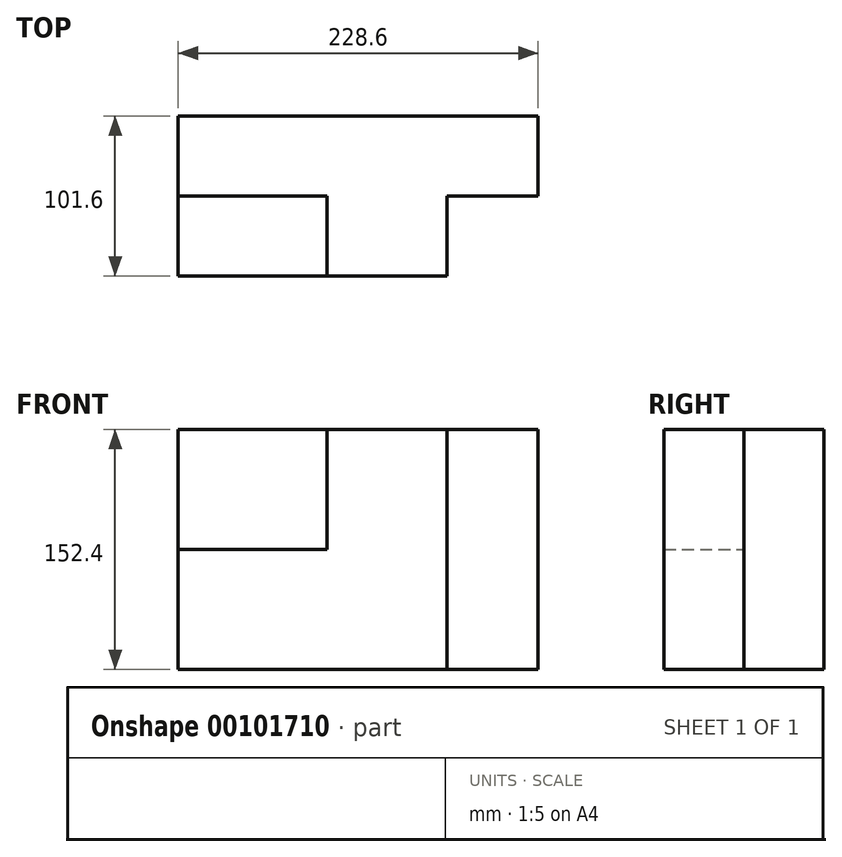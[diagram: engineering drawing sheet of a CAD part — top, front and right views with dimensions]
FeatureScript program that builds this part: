
annotation { "Feature Type Name" : "Feature", "Feature Type Description" : "" }
export const myFeature = defineFeature(function(context is Context, id is Id, definition is map)
    precondition{}
    {
        {
            var Q0;
            Q0=qCreatedBy(makeId("Front.planeOp"),FACE);
            var sketch = newSketch(context, id + "F0", { "sketchPlane" : qUnion([Q0])});
            skLineSegment(sketch, "E0", {"start": v(-118.58, 68.69) * mm, "end": v(-118.58, -83.71) * mm});
            skLineSegment(sketch, "E1", {"start": v(-118.58, -83.71) * mm, "end": v(110.02, -83.71) * mm});
            skLineSegment(sketch, "E2", {"start": v(110.02, -83.71) * mm, "end": v(110.02, 68.69) * mm});
            skLineSegment(sketch, "E3", {"start": v(110.02, 68.69) * mm, "end": v(-118.58, 68.69) * mm});
            skSolve(sketch);
        }
        {
            var Q0;
            Q0=makeQuery(id+"F0.imprint","IMPRINT",FACE,{"disambiguationData":[TD([[makeQuery(id+"F0.imprint","IMPRINT",EDGE,{"derivedFrom":sQuery(id+"F0.wireOp",EDGE,"E0")}),1.0]])]});
            extrude(context, id + "F1", {"entities" : qUnion([Q0]), "depth" : 50.8 * mm});
        }
        {
            var Q0;
            Q0=makeQuery(id+"F1.opExtrude","CAP_FACE",FACE,{"disambiguationData":[OSD([sQuery(id+"F0.wireOp",EDGE,"E0"),sQuery(id+"F0.wireOp",EDGE,"E1"),sQuery(id+"F0.wireOp",EDGE,"E2"),sQuery(id+"F0.wireOp",EDGE,"E3")])],"isStart":false});
            var sketch = newSketch(context, id + "F2", { "sketchPlane" : qUnion([Q0])});
            skLineSegment(sketch, "E4.bottom", {"start": v(-24.16, 68.69) * mm, "end": v(52.04, 68.69) * mm});
            skLineSegment(sketch, "E4.top", {"start": v(-24.16, -83.71) * mm, "end": v(52.04, -83.71) * mm});
            skLineSegment(sketch, "E4.left", {"start": v(-24.16, 68.69) * mm, "end": v(-24.16, -83.71) * mm});
            skLineSegment(sketch, "E4.right", {"start": v(52.04, 68.69) * mm, "end": v(52.04, -83.71) * mm});
            skSolve(sketch);
        }
        {
            var Q0;
            Q0=makeQuery(id+"F2.imprint","IMPRINT",FACE,{"disambiguationData":[TD([[makeQuery(id+"F2.imprint","IMPRINT",EDGE,{"derivedFrom":sQuery(id+"F2.wireOp",EDGE,"E4.bottom")}),1.0]])]});
            extrude(context, id + "F3", {"entities" : qUnion([Q0]), "operationType" : NewBodyOperationType.ADD, "depth" : 50.8 * mm});
        }
        {
            var Q0;
            {var subQ0=sQuery(id+"F0.wireOp",EDGE,"E3");var subQ1=sQuery(id+"F0.wireOp",EDGE,"E1");var subQ2=sQuery(id+"F0.wireOp",EDGE,"E0");Q0=makeQuery(id+"F3.boolean.opBoolean","SPLIT",FACE,{"disambiguationData":[TD([makeQuery(id+"F1.opExtrude","SWEPT_FACE",FACE,{"disambiguationData":[OSD([subQ2])]})])],"derivedFrom":makeQuery(id+"F1.opExtrude","CAP_FACE",FACE,{"disambiguationData":[OSD([subQ2,subQ1,sQuery(id+"F0.wireOp",EDGE,"E2"),subQ0])],"isStart":false})});}
            var sketch = newSketch(context, id + "F4", { "sketchPlane" : qUnion([Q0])});
            skLineSegment(sketch, "E5.bottom", {"start": v(-118.58, -83.71) * mm, "end": v(-24.16, -83.71) * mm});
            skLineSegment(sketch, "E5.top", {"start": v(-118.58, -7.51) * mm, "end": v(-24.16, -7.51) * mm});
            skLineSegment(sketch, "E5.left", {"start": v(-118.58, -83.71) * mm, "end": v(-118.58, -7.51) * mm});
            skLineSegment(sketch, "E5.right", {"start": v(-24.16, -83.71) * mm, "end": v(-24.16, -7.51) * mm});
            skSolve(sketch);
        }
        {
            var Q0;
            Q0=makeQuery(id+"F4.imprint","IMPRINT",FACE,{"disambiguationData":[TD([[makeQuery(id+"F4.imprint","IMPRINT",EDGE,{"derivedFrom":sQuery(id+"F4.wireOp",EDGE,"E5.bottom")}),1.0]])]});
            extrude(context, id + "F5", {"entities" : qUnion([Q0]), "operationType" : NewBodyOperationType.ADD, "depth" : 50.8 * mm});
        }
    });
